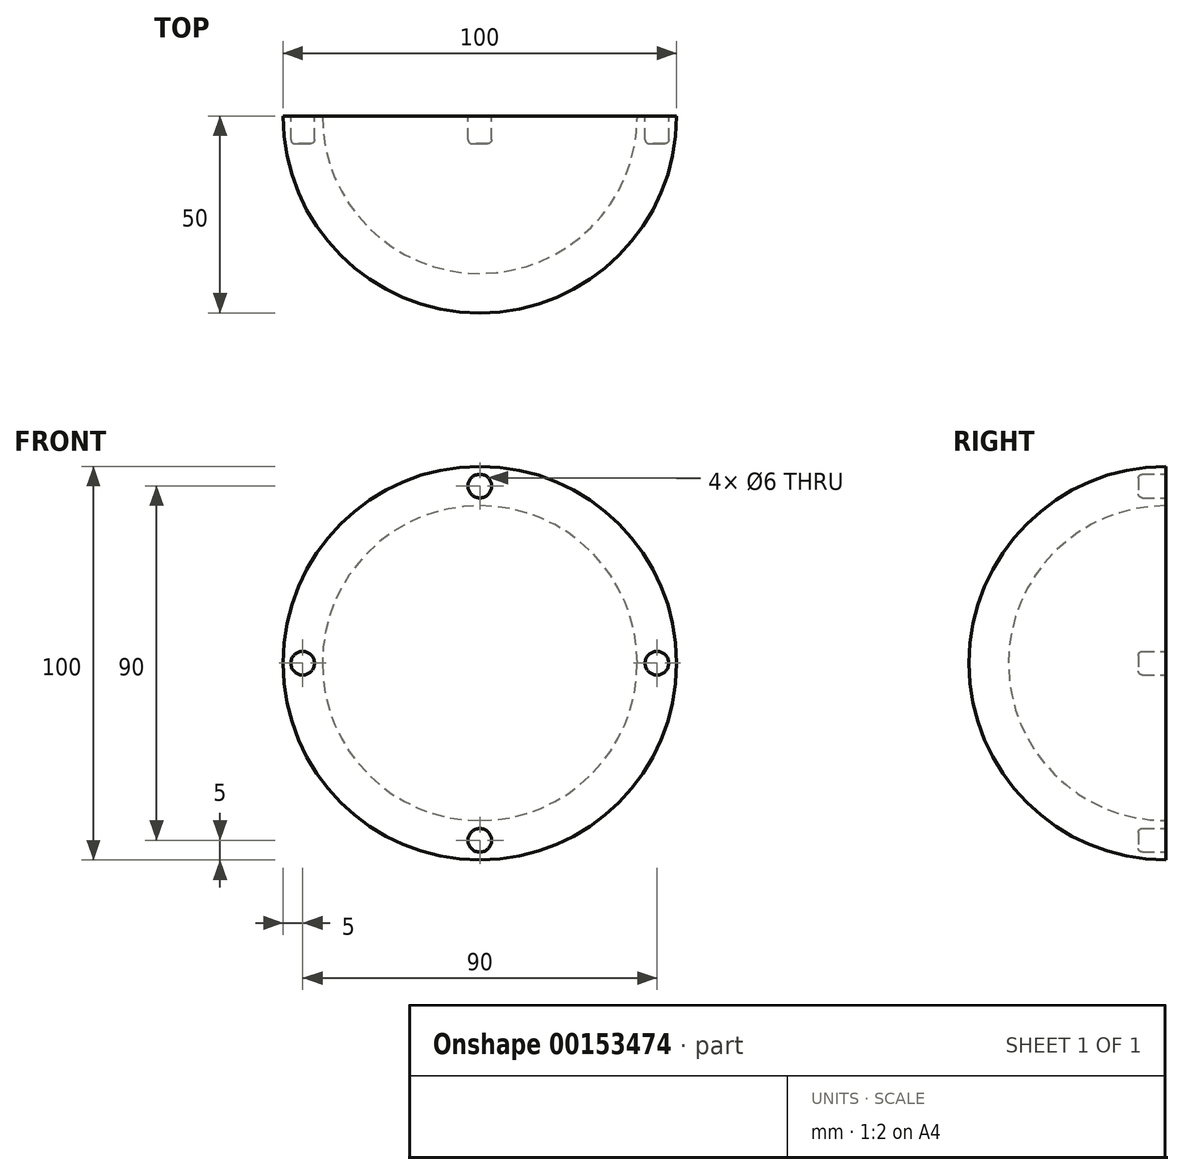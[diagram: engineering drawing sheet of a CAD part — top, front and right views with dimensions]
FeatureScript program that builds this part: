
annotation { "Feature Type Name" : "Feature", "Feature Type Description" : "" }
export const myFeature = defineFeature(function(context is Context, id is Id, definition is map)
    precondition{}
    {
        {
            var Q0;
            Q0=qCreatedBy(makeId("Front.planeOp"),FACE);
            var sketch = newSketch(context, id + "F0", { "sketchPlane" : qUnion([Q0])});
            skArc(sketch, "E0", {"start": v(-50, 0) * mm, "mid": v(0, -50) * mm, "end": v(50, 0) * mm});
            skLineSegment(sketch, "E1", {"start": v(-40, 0) * mm, "end": v(-50, 0) * mm});
            skCircle(sketch, "E2", {"center": v(0, 0) * mm, "radius": 40 * mm});
            skLineSegment(sketch, "E3", {"start": v(50, 0) * mm, "end": v(40, 0) * mm});
            skSolve(sketch);
        }
        {
            var Q0;
            Q0=qCreatedBy(makeId("Right.planeOp"),FACE);
            var sketch = newSketch(context, id + "F1", { "sketchPlane" : qUnion([Q0])});
            skLineSegment(sketch, "E4", {"start": v(0, 56.62) * mm, "end": v(0, -56.38) * mm, "construction": true});
            skSolve(sketch);
        }
        {
            var Q0;
            Q0=qCreatedBy(makeId("Front.planeOp"),FACE);
            var sketch = newSketch(context, id + "F2", { "sketchPlane" : qUnion([Q0])});
            skLineSegment(sketch, "E5", {"start": v(-74.79, 0) * mm, "end": v(75.26, 0) * mm, "construction": true});
            skSolve(sketch);
        }
        {
            var Q0;
            Q0=makeQuery(id+"F0.imprint","IMPRINT",FACE,{"disambiguationData":[TD([[makeQuery(id+"F0.imprint","IMPRINT",EDGE,{"derivedFrom":sQuery(id+"F0.wireOp",EDGE,"E0")}),1.0]])]});
            var Q1;
            Q1=sQuery(id+"F2.wireOp",EDGE,"E5");
            revolve(context, id + "F3", {"entities" : qUnion([Q0]), "axis" : qUnion([Q1]), "revolveType" : RevolveType.FULL});
        }
        {
            var Q0;
            Q0=qCreatedBy(makeId("Front.planeOp"),FACE);
            var sketch = newSketch(context, id + "F4", { "sketchPlane" : qUnion([Q0])});
            skLineSegment(sketch, "E6.bottom", {"start": v(-30, 30) * mm, "end": v(30, 30) * mm});
            skLineSegment(sketch, "E6.top", {"start": v(-30, -30) * mm, "end": v(30, -30) * mm});
            skLineSegment(sketch, "E6.left", {"start": v(-30, 30) * mm, "end": v(-30, -30) * mm});
            skLineSegment(sketch, "E6.right", {"start": v(30, 30) * mm, "end": v(30, -30) * mm});
            skSolve(sketch);
        }
        {
            var Q0;
            Q0=qSketchRegion(id+"F4",true);
            extrude(context, id + "F5", {"entities" : qUnion([Q0]), "operationType" : NewBodyOperationType.REMOVE, "oppositeDirection" : true, "depth" : 30 * mm});
        }
        {
            var Q0;
            Q0=qCreatedBy(makeId("Front.planeOp"),FACE);
            var sketch = newSketch(context, id + "F6", { "sketchPlane" : qUnion([Q0])});
            skLineSegment(sketch, "E7.bottom", {"start": v(-75, 75) * mm, "end": v(75, 75) * mm});
            skLineSegment(sketch, "E7.top", {"start": v(-75, -75) * mm, "end": v(75, -75) * mm});
            skLineSegment(sketch, "E7.left", {"start": v(-75, 75) * mm, "end": v(-75, -75) * mm});
            skLineSegment(sketch, "E7.right", {"start": v(75, 75) * mm, "end": v(75, -75) * mm});
            skSolve(sketch);
        }
        {
            var Q0;
            Q0=makeQuery(id+"F6.imprint","IMPRINT",FACE,{"disambiguationData":[TD([[makeQuery(id+"F6.imprint","IMPRINT",EDGE,{"derivedFrom":sQuery(id+"F6.wireOp",EDGE,"E7.bottom")}),-1.0]])]});
            extrude(context, id + "F7", {"entities" : qUnion([Q0]), "operationType" : NewBodyOperationType.REMOVE, "oppositeDirection" : true, "depth" : 65.75 * mm});
        }
        {
            var Q0;
            {var subQ0=makeQuery(id+"F3.opRevolve","SWEPT_FACE",FACE,{"disambiguationData":[OSD([sQuery(id+"F0.wireOp",EDGE,"E2")])]});var subQ1=sQuery(id+"F4.wireOp",EDGE,"E6.top");var subQ2=makeQuery(id+"F5.opExtrude","SWEPT_FACE",FACE,{"disambiguationData":[OSD([subQ1])]});var subQ3=sQuery(id+"F4.wireOp",EDGE,"E6.right");var subQ4=makeQuery(id+"F5.opExtrude","SWEPT_FACE",FACE,{"disambiguationData":[OSD([subQ3])]});var subQ5=sQuery(id+"F4.wireOp",EDGE,"E6.left");var subQ6=sQuery(id+"F4.wireOp",EDGE,"E6.bottom");var subQ7=makeQuery(id+"F5.opExtrude","CAP_FACE",FACE,{"disambiguationData":[OSD([subQ6,subQ1,subQ5,subQ3])],"isStart":true});var subQ8=makeQuery(id+"F5.opExtrude","SWEPT_FACE",FACE,{"disambiguationData":[OSD([subQ5])]});var subQ9=makeQuery(id+"F5.opExtrude","SWEPT_FACE",FACE,{"disambiguationData":[OSD([subQ6])]});Q0=makeQuery(id+"F7.boolean.opBoolean","MERGE",FACE,{"derivedFrom":[makeQuery(id+"F5.boolean.opBoolean","COPY",FACE,{"disambiguationData":[TD([subQ0,subQ9,subQ8])],"derivedFrom":subQ7}),makeQuery(id+"F5.boolean.opBoolean","COPY",FACE,{"disambiguationData":[TD([subQ0,subQ9,subQ4])],"derivedFrom":subQ7}),makeQuery(id+"F5.boolean.opBoolean","COPY",FACE,{"disambiguationData":[TD([subQ0,subQ2,subQ8])],"derivedFrom":subQ7}),makeQuery(id+"F5.boolean.opBoolean","COPY",FACE,{"disambiguationData":[TD([subQ0,subQ2,subQ4])],"derivedFrom":subQ7}),makeQuery(id+"F7.opExtrude","CAP_FACE",FACE,{"disambiguationData":[OSD([sQuery(id+"F6.wireOp",EDGE,"E7.bottom"),sQuery(id+"F6.wireOp",EDGE,"E7.top"),sQuery(id+"F6.wireOp",EDGE,"E7.left"),sQuery(id+"F6.wireOp",EDGE,"E7.right")])],"isStart":true})]});}
            var sketch = newSketch(context, id + "F8", { "sketchPlane" : qUnion([Q0])});
            skCircle(sketch, "E8", {"center": v(0, 0) * mm, "radius": 45 * mm, "construction": true});
            skLineSegment(sketch, "E9", {"start": v(0, 0) * mm, "end": v(-50, 0) * mm, "construction": true});
            skCircle(sketch, "E10", {"center": v(-45, 0) * mm, "radius": 3 * mm});
            skCircle(sketch, "E11.1.0", {"center": v(0, -45) * mm, "radius": 3 * mm});
            skCircle(sketch, "E11.2.0", {"center": v(45, 0) * mm, "radius": 3 * mm});
            skCircle(sketch, "E11.3.0", {"center": v(0, 45) * mm, "radius": 3 * mm});
            skSolve(sketch);
        }
        {
            var Q0;
            Q0=makeQuery(id+"F8.imprint","IMPRINT",FACE,{"disambiguationData":[TD([[makeQuery(id+"F8.imprint","IMPRINT",EDGE,{"derivedFrom":sQuery(id+"F8.wireOp",EDGE,"E11.2.0")}),1.0]])]});
            var Q1;
            Q1=makeQuery(id+"F8.imprint","IMPRINT",FACE,{"disambiguationData":[TD([[makeQuery(id+"F8.imprint","IMPRINT",EDGE,{"derivedFrom":sQuery(id+"F8.wireOp",EDGE,"E10")}),1.0]])]});
            var Q2;
            Q2=makeQuery(id+"F8.imprint","IMPRINT",FACE,{"disambiguationData":[TD([[makeQuery(id+"F8.imprint","IMPRINT",EDGE,{"derivedFrom":sQuery(id+"F8.wireOp",EDGE,"E11.1.0")}),1.0]])]});
            var Q3;
            Q3=makeQuery(id+"F8.imprint","IMPRINT",FACE,{"disambiguationData":[TD([[makeQuery(id+"F8.imprint","IMPRINT",EDGE,{"derivedFrom":sQuery(id+"F8.wireOp",EDGE,"E11.3.0")}),1.0]])]});
            extrude(context, id + "F9", {"entities" : qUnion([Q0, Q1, Q2, Q3]), "operationType" : NewBodyOperationType.REMOVE, "oppositeDirection" : true, "depth" : 7 * mm});
        }
        {
            var Q0;
            Q0=makeQuery(id+"F9.boolean.opBoolean","COPY",EDGE,{"derivedFrom":makeQuery(id+"F9.opExtrude","CAP_EDGE",EDGE,{"disambiguationData":[OSD([sQuery(id+"F8.wireOp",EDGE,"E10")])],"isStart":true})});
            var Q1;
            Q1=makeQuery(id+"F9.boolean.opBoolean","COPY",EDGE,{"derivedFrom":makeQuery(id+"F9.opExtrude","CAP_EDGE",EDGE,{"disambiguationData":[OSD([sQuery(id+"F8.wireOp",EDGE,"E10")])],"isStart":false})});
            var Q2;
            Q2=makeQuery(id+"F9.boolean.opBoolean","COPY",EDGE,{"derivedFrom":makeQuery(id+"F9.opExtrude","CAP_EDGE",EDGE,{"disambiguationData":[OSD([sQuery(id+"F8.wireOp",EDGE,"E11.3.0")])],"isStart":true})});
            var Q3;
            Q3=makeQuery(id+"F9.boolean.opBoolean","COPY",EDGE,{"derivedFrom":makeQuery(id+"F9.opExtrude","CAP_EDGE",EDGE,{"disambiguationData":[OSD([sQuery(id+"F8.wireOp",EDGE,"E11.3.0")])],"isStart":false})});
            var Q4;
            Q4=makeQuery(id+"F9.boolean.opBoolean","COPY",EDGE,{"derivedFrom":makeQuery(id+"F9.opExtrude","CAP_EDGE",EDGE,{"disambiguationData":[OSD([sQuery(id+"F8.wireOp",EDGE,"E11.2.0")])],"isStart":true})});
            var Q5;
            Q5=makeQuery(id+"F9.boolean.opBoolean","COPY",EDGE,{"derivedFrom":makeQuery(id+"F9.opExtrude","CAP_EDGE",EDGE,{"disambiguationData":[OSD([sQuery(id+"F8.wireOp",EDGE,"E11.2.0")])],"isStart":false})});
            var Q6;
            Q6=makeQuery(id+"F9.boolean.opBoolean","COPY",EDGE,{"derivedFrom":makeQuery(id+"F9.opExtrude","CAP_EDGE",EDGE,{"disambiguationData":[OSD([sQuery(id+"F8.wireOp",EDGE,"E11.1.0")])],"isStart":true})});
            var Q7;
            Q7=makeQuery(id+"F9.boolean.opBoolean","COPY",EDGE,{"derivedFrom":makeQuery(id+"F9.opExtrude","CAP_EDGE",EDGE,{"disambiguationData":[OSD([sQuery(id+"F8.wireOp",EDGE,"E11.1.0")])],"isStart":false})});
            fillet(context, id + "F10", {"entities" : qUnion([Q0, Q1, Q2, Q3, Q4, Q5, Q6, Q7]), "radius" : 1 * mm, "tangentPropagation" : true, "allowEdgeOverflow" : false});
        }
    });
